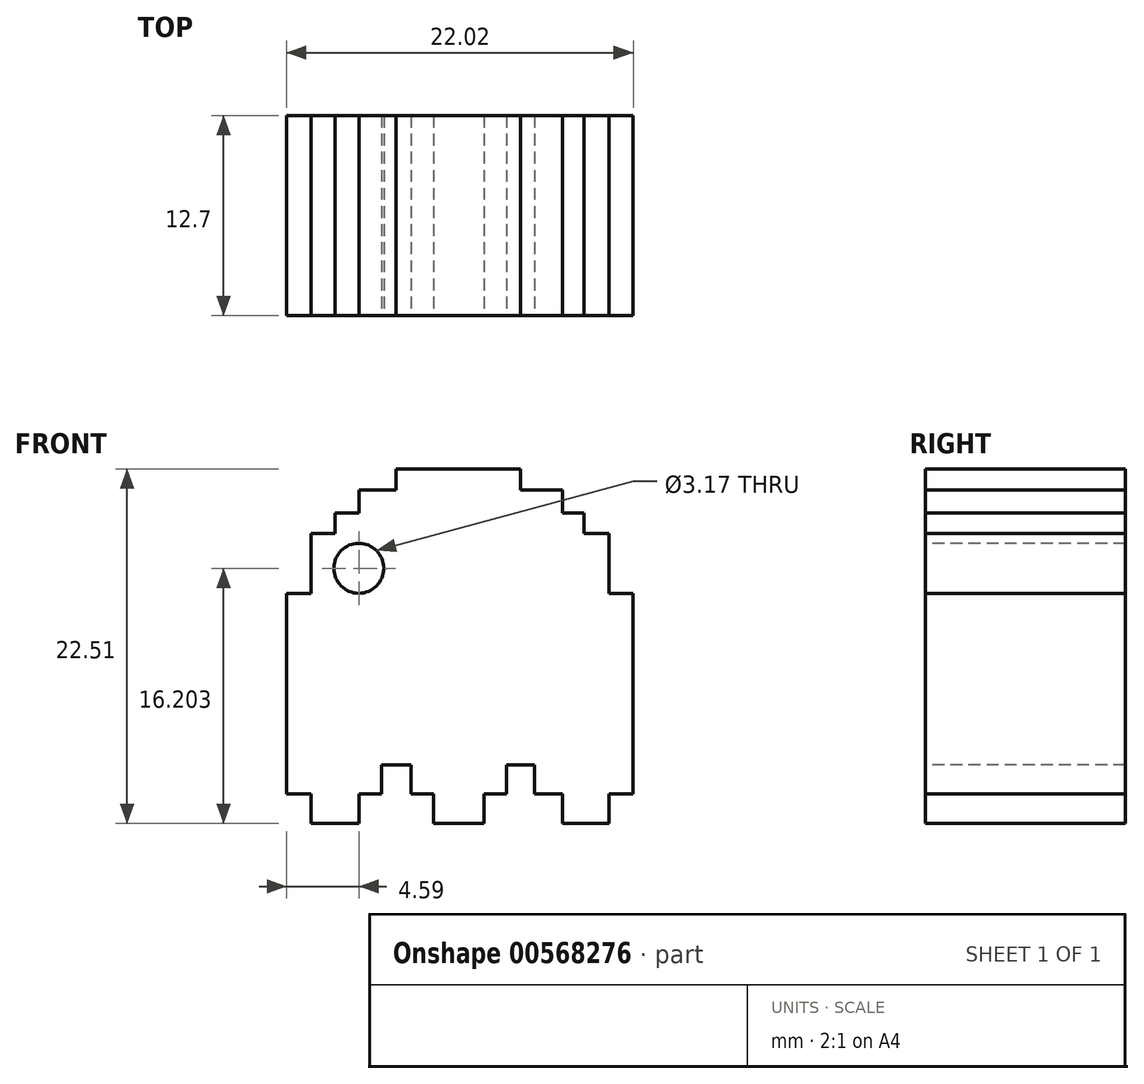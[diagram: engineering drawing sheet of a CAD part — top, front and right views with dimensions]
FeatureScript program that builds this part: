
annotation { "Feature Type Name" : "Feature", "Feature Type Description" : "" }
export const myFeature = defineFeature(function(context is Context, id is Id, definition is map)
    precondition{}
    {
        {
            var Q0;
            Q0=qCreatedBy(makeId("Front.planeOp"),FACE);
            var sketch = newSketch(context, id + "F0", { "sketchPlane" : qUnion([Q0])});
            skLineSegment(sketch, "E0", {"start": v(0, 0) * mm, "end": v(0, 25.4) * mm});
            skLineSegment(sketch, "E1", {"start": v(0, 25.4) * mm, "end": v(25.4, 25.4) * mm});
            skLineSegment(sketch, "E2", {"start": v(25.4, 25.4) * mm, "end": v(25.4, 0) * mm});
            skLineSegment(sketch, "E3", {"start": v(25.4, 0) * mm, "end": v(0, 0) * mm});
            skSolve(sketch);
        }
        {
            var Q0;
            Q0 = qSketchRegion(id + "F0", true);
            extrude(context, id + "F1", {"entities" : qUnion([Q0]), "depth" : 12.7 * mm, "offsetDistance" : 25.4 * mm});
        }
        {
            var Q0;
            Q0=makeQuery(id+"F1.opExtrude","CAP_FACE",FACE,{"disambiguationData":[OSD([sQuery(id+"F0.wireOp",EDGE,"E0"),sQuery(id+"F0.wireOp",EDGE,"E1"),sQuery(id+"F0.wireOp",EDGE,"E2"),sQuery(id+"F0.wireOp",EDGE,"E3")])],"isStart":false});
            var sketch = newSketch(context, id + "F2", { "sketchPlane" : qUnion([Q0])});
            skLineSegment(sketch, "E4", {"start": v(3.2, 0) * mm, "end": v(6.25, 0) * mm});
            skLineSegment(sketch, "E5", {"start": v(6.25, 0) * mm, "end": v(6.25, 1.88) * mm});
            skLineSegment(sketch, "E6", {"start": v(6.25, 1.88) * mm, "end": v(7.68, 1.88) * mm});
            skLineSegment(sketch, "E7", {"start": v(7.68, 1.88) * mm, "end": v(7.68, 3.7) * mm});
            skLineSegment(sketch, "E8", {"start": v(7.68, 3.7) * mm, "end": v(9.56, 3.7) * mm});
            skLineSegment(sketch, "E9", {"start": v(9.56, 3.7) * mm, "end": v(9.56, 1.88) * mm});
            skLineSegment(sketch, "E10", {"start": v(9.56, 1.88) * mm, "end": v(10.99, 1.88) * mm});
            skLineSegment(sketch, "E11", {"start": v(10.99, 1.88) * mm, "end": v(10.99, 0) * mm});
            skLineSegment(sketch, "E12", {"start": v(10.99, 0) * mm, "end": v(14.2, 0) * mm});
            skLineSegment(sketch, "E13", {"start": v(14.2, 0) * mm, "end": v(14.2, 1.88) * mm});
            skLineSegment(sketch, "E14", {"start": v(14.2, 1.88) * mm, "end": v(15.63, 1.88) * mm});
            skLineSegment(sketch, "E15", {"start": v(15.63, 1.88) * mm, "end": v(15.63, 3.7) * mm});
            skLineSegment(sketch, "E16", {"start": v(15.63, 3.7) * mm, "end": v(17.4, 3.7) * mm});
            skLineSegment(sketch, "E17", {"start": v(17.4, 3.7) * mm, "end": v(17.4, 1.88) * mm});
            skLineSegment(sketch, "E18", {"start": v(17.4, 1.88) * mm, "end": v(19.18, 1.88) * mm});
            skLineSegment(sketch, "E19", {"start": v(19.18, 1.88) * mm, "end": v(19.18, 0) * mm});
            skLineSegment(sketch, "E20", {"start": v(19.18, 0) * mm, "end": v(22.15, 0) * mm});
            skLineSegment(sketch, "E21", {"start": v(22.15, 0) * mm, "end": v(22.15, 1.88) * mm});
            skLineSegment(sketch, "E22", {"start": v(22.15, 1.88) * mm, "end": v(23.68, 1.88) * mm});
            skLineSegment(sketch, "E23", {"start": v(3.2, 0) * mm, "end": v(3.2, 1.88) * mm});
            skLineSegment(sketch, "E24", {"start": v(3.2, 1.88) * mm, "end": v(1.66, 1.88) * mm});
            skLineSegment(sketch, "E25", {"start": v(1.66, 1.88) * mm, "end": v(1.66, 14.62) * mm});
            skLineSegment(sketch, "E26", {"start": v(1.66, 14.62) * mm, "end": v(3.2, 14.62) * mm});
            skLineSegment(sketch, "E27", {"start": v(3.2, 14.62) * mm, "end": v(3.2, 18.42) * mm});
            skLineSegment(sketch, "E28", {"start": v(3.2, 18.42) * mm, "end": v(4.73, 18.42) * mm});
            skPoint(sketch, "E28.endSnap0", {"position": v(4.73, 0) * mm});
            skLineSegment(sketch, "E29", {"start": v(4.73, 18.42) * mm, "end": v(4.73, 19.7) * mm});
            skLineSegment(sketch, "E30", {"start": v(4.73, 19.7) * mm, "end": v(6.25, 19.7) * mm});
            skLineSegment(sketch, "E31", {"start": v(6.25, 19.7) * mm, "end": v(6.25, 21.18) * mm});
            skLineSegment(sketch, "E32", {"start": v(6.25, 21.18) * mm, "end": v(8.62, 21.18) * mm});
            skPoint(sketch, "E32.endSnap0", {"position": v(8.62, 3.7) * mm});
            skLineSegment(sketch, "E33", {"start": v(8.62, 21.18) * mm, "end": v(8.62, 22.51) * mm});
            skLineSegment(sketch, "E34", {"start": v(8.62, 22.51) * mm, "end": v(16.52, 22.51) * mm});
            skPoint(sketch, "E34.endSnap0", {"position": v(16.52, 3.7) * mm});
            skLineSegment(sketch, "E35", {"start": v(16.52, 22.51) * mm, "end": v(16.52, 21.18) * mm});
            skLineSegment(sketch, "E36", {"start": v(16.52, 21.18) * mm, "end": v(19.18, 21.18) * mm});
            skLineSegment(sketch, "E37", {"start": v(19.18, 21.18) * mm, "end": v(19.18, 19.7) * mm});
            skLineSegment(sketch, "E38", {"start": v(19.18, 19.7) * mm, "end": v(20.57, 19.7) * mm});
            skLineSegment(sketch, "E39", {"start": v(20.57, 19.7) * mm, "end": v(20.57, 18.42) * mm});
            skLineSegment(sketch, "E40", {"start": v(20.57, 18.42) * mm, "end": v(22.15, 18.42) * mm});
            skLineSegment(sketch, "E41", {"start": v(22.15, 18.42) * mm, "end": v(22.15, 14.62) * mm});
            skLineSegment(sketch, "E42", {"start": v(22.15, 14.62) * mm, "end": v(23.68, 14.62) * mm});
            skLineSegment(sketch, "E43", {"start": v(23.68, 14.62) * mm, "end": v(23.68, 1.88) * mm});
            skSolve(sketch);
        }
        {
            var Q0;
            {var subQ1=sQuery(id+"F2.wireOp",EDGE,"E21");Q0=makeQuery(id+"F2.imprint","IMPRINT",FACE,{"disambiguationData":[TD([[makeQuery(id+"F2.imprint","IMPRINT",EDGE,{"derivedFrom":subQ1}),-1.0]])]});}
            var Q1;
            {var subQ0=sQuery(id+"F2.wireOp",EDGE,"E13");Q1=makeQuery(id+"F2.imprint","IMPRINT",FACE,{"disambiguationData":[TD([[makeQuery(id+"F2.imprint","IMPRINT",EDGE,{"derivedFrom":subQ0}),-1.0]])]});}
            var Q2;
            {var subQ0=sQuery(id+"F2.wireOp",EDGE,"E5");Q2=makeQuery(id+"F2.imprint","IMPRINT",FACE,{"disambiguationData":[TD([[makeQuery(id+"F2.imprint","IMPRINT",EDGE,{"derivedFrom":subQ0}),-1.0]])]});}
            extrude(context, id + "F3", {"entities" : qUnion([Q0, Q1, Q2]), "operationType" : NewBodyOperationType.REMOVE, "oppositeDirection" : true, "depth" : 12.7 * mm, "offsetDistance" : 25.4 * mm});
        }
        {
            var Q0;
            Q0=makeQuery(id+"F1.opExtrude","CAP_FACE",FACE,{"disambiguationData":[OSD([sQuery(id+"F0.wireOp",EDGE,"E0"),sQuery(id+"F0.wireOp",EDGE,"E1"),sQuery(id+"F0.wireOp",EDGE,"E2"),sQuery(id+"F0.wireOp",EDGE,"E3")])],"isStart":false});
            var sketch = newSketch(context, id + "F4", { "sketchPlane" : qUnion([Q0])});
            skCircle(sketch, "E44", {"center": v(6.25, 16.2) * mm, "radius": 1.59 * mm});
            skSolve(sketch);
        }
        {
            var Q0;
            Q0 = qSketchRegion(id + "F4", true);
            extrude(context, id + "F5", {"entities" : qUnion([Q0]), "operationType" : NewBodyOperationType.REMOVE, "oppositeDirection" : true, "depth" : 12.7 * mm, "offsetDistance" : 25.4 * mm});
        }
    });
